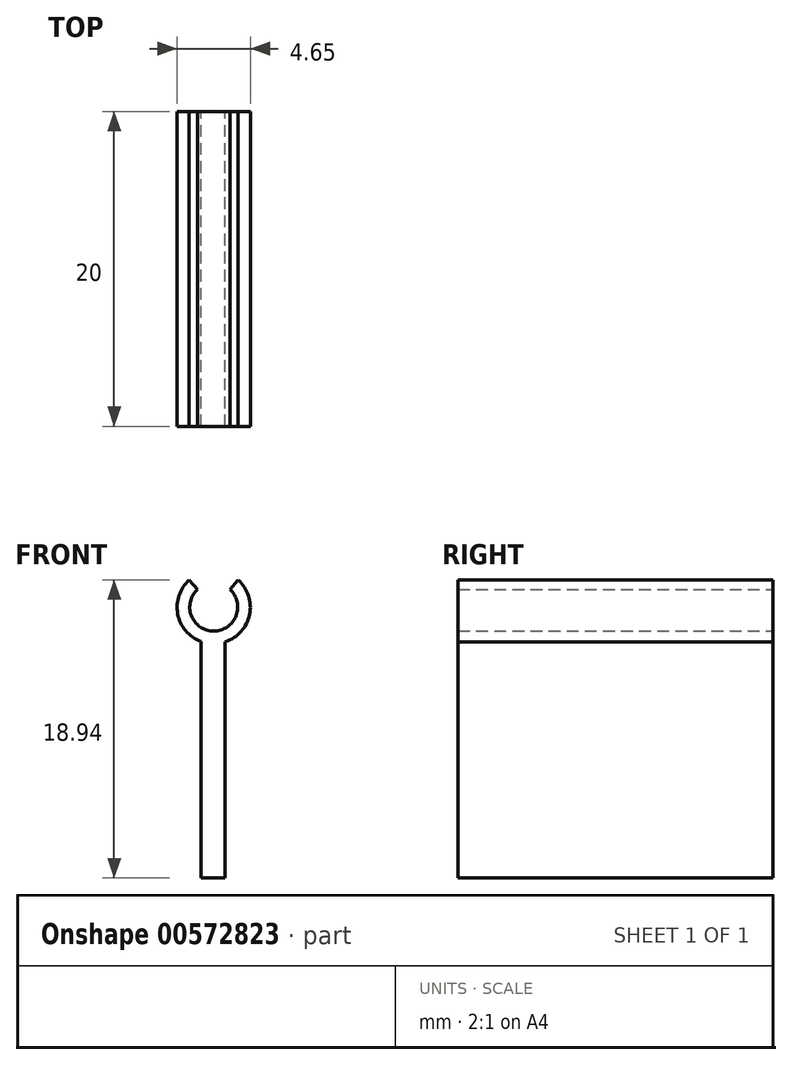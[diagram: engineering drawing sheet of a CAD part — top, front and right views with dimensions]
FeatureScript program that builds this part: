
annotation { "Feature Type Name" : "Feature", "Feature Type Description" : "" }
export const myFeature = defineFeature(function(context is Context, id is Id, definition is map)
    precondition{}
    {
        {
            var Q0;
            Q0=qCreatedBy(makeId("Front.planeOp"),FACE);
            var sketch = newSketch(context, id + "F0", { "sketchPlane" : qUnion([Q0])});
            skCircle(sketch, "E0", {"center": v(0, 0) * mm, "radius": 1.52 * mm});
            skArc(sketch, "E1", {"start": v(0.73, -2.2) * mm, "mid": v(0.04, 2.32) * mm, "end": v(-0.82, -2.18) * mm});
            skLineSegment(sketch, "E2.top", {"start": v(-0.82, -17.2) * mm, "end": v(0.73, -17.2) * mm});
            skLineSegment(sketch, "E2.left", {"start": v(-0.82, -2.18) * mm, "end": v(-0.82, -17.2) * mm});
            skLineSegment(sketch, "E2.right", {"start": v(0.73, -2.2) * mm, "end": v(0.73, -17.2) * mm});
            skSolve(sketch);
        }
        {
            var Q0;
            Q0 = qSketchRegion(id + "F0", true);
            extrude(context, id + "F1", {"entities" : qUnion([Q0]), "depth" : 20 * mm, "offsetDistance" : 25 * mm});
        }
        {
            var Q0;
            Q0=makeQuery(id+"F1.opExtrude","CAP_FACE",FACE,{"disambiguationData":[OSD([sQuery(id+"F0.wireOp",EDGE,"E0"),sQuery(id+"F0.wireOp",EDGE,"E1"),sQuery(id+"F0.wireOp",EDGE,"E2.top"),sQuery(id+"F0.wireOp",EDGE,"E2.left"),sQuery(id+"F0.wireOp",EDGE,"E2.right")])],"isStart":false});
            var sketch = newSketch(context, id + "F2", { "sketchPlane" : qUnion([Q0])});
            skLineSegment(sketch, "E3", {"start": v(-4.5, 5) * mm, "end": v(0, 0) * mm});
            skLineSegment(sketch, "E4", {"start": v(0, 0) * mm, "end": v(4.5, 5) * mm});
            skLineSegment(sketch, "E5", {"start": v(-4.5, 5) * mm, "end": v(0, 5.45) * mm});
            skLineSegment(sketch, "E6", {"start": v(0, 5.45) * mm, "end": v(4.5, 5) * mm});
            skSolve(sketch);
        }
        {
            var Q0;
            Q0 = qSketchRegion(id + "F2", true);
            extrude(context, id + "F3", {"entities" : qUnion([Q0]), "operationType" : NewBodyOperationType.REMOVE, "oppositeDirection" : true, "depth" : 25 * mm, "offsetDistance" : 25 * mm});
        }
    });
